# Revit family: LTC-4RDW-S
name_source: partatom
category: Lighting Fixtures
revit_build: Autodesk Revit 2017 (Build: 20160225_1515(x64)
units: mm (PartAtom-declared; Revit-internal decimal feet)

## family parameters
Cut with Voids When Loaded = No
Host = Face
Light Source = Yes
OmniClass Number = 23.80.70.11.14.11
OmniClass Title = Downlights
Part Type = Normal
Room Calculation Point = No
Round Connector Dimension = Use Diameter
Shared = Yes

## types (2) — shared parameters
Apparent Load = 52 VA
Ceiling Cutout = 6.25 "
Color Filter = 16777215
Connector Description = Lighting Connector
Cutout Radius = 3.13 "
Default Elevation = 48 "
Description = Liteistry 4 inch Round cylinder with color tuning
Dimming Lamp Color Temperature Shift = <None>
Emit Shape Visible in Rendering = Yes
Emit from Circle Diameter = 5.6 "
Features = • 4inch architectural LED downlight and wall wash cylinder delivering 600–1500 lm 
• 4 beam distributions from 0.4 to 1.2 Spacing Criteria 
• Quiet reflector appearance with 50º optical cutoff
 • SpectraSync™ Color Tuning technology allows the flexibility to tailor CCT to aesthetic preferences • Available in Dim To Warm (2200K-3000K) or Tunable White (2700K-5000K or 2700K-6500K), 90+ CRI 
• Available in Surface, Wall, Pendant, or Cable/Cord Mount configurations
• Versatile canopy options for recessed and surface-mounted J-box applications 
• Standard with 0-10V dimming to 5%
Frequency = 60 Hz
Glass = Hubbell - White Glass
Is 120V = Yes
Is 277V = No
Lamp = LED's
Load Classification = Lighting
Manufacturer = Prescolite
Model = LTC-4RDW
Photometric Notes = More IES files download on Photometric Web Link
Photometric Web File = LTC-4RD-P-20L35K8MD-DM1-S-BL.ies
Photometric Web Link = https://www.hubbell.com
Product Documentation Link = https://hubbellcdn.com
Product Material = Paint - Hubbell - Carbon Black
Product Page URL = https://www.hubbell.com
Reflector Finish = Paint - Hubbell - Carbon Black
Tilt Angle = -90.00°
URL = https://www.hubbell.com
Voltage = 120 V

## per-type parameters (varying)
| type | Canopy Depth | Canopy Diameter | S |
| LTC-4RDW-SCC | 3 " | 5.75 " | No |
| LTC-4RDW-S | 0.2 " | 5.6 " | Yes |

## geometry (parser evidence)
native form markers: Blend x4, Sweep x2
no freeform markers — native parametric forms only
